# Revit family: Toilet_Seat_Tissue_Dispenser-Bobrick-ClassicSeries-B-3479
name_source: partatom
category: Specialty Equipment
revit_build: Autodesk Revit 2014 (Build: 20130308_1515(x64)
units: mm (PartAtom-declared; Revit-internal decimal feet)

## types (1)
- B-3479
    ADA Compliant = Yes
    Assembly Code = E1010900
    Default Elevation = 60"
    Description = Bobrick ClassicSeries® Surface-Mounted Seat-Cover and Toilet Tissue Dispenser
    Height = 30 7/8"
    Installation Type = Wall Mounted
    Length = 4 3/16"
    Manufacturer = Bobrick Washroom Equipment, Inc.
    Material = Stainless Steel-Bobrick-Type 304-Satin
    Model = B-3479
    Price = Prices may vary. Please consult Manufacturer Representative for most up-to-date price list.
    Product Documentation Link = http://www.bobrick.com
    Product Page URL = http://www.bobrick.com
    Specification = Surface-mounted toilet-seat-cover and toilet tissue dispenser shall be type-304 stainless steel; exposed surfaces shall have satin finish. Toilet tissue dispenser shall be ABS plastic. Flange shall be drawn and beveled, one-piece, seamless construction. Unit shall be mounted on side wall of single toilet compartment. Doors shall be one-piece, seamless construction; secured to unit with a full-length stainless steel piano-hinge; and equipped with tumbler locks keyed like other Bobrick washroom accessories. Toilet-seat-cover dispenser shall hold 500 paper covers. Unit shall be equipped with two theft-resistant, heavy-duty ABS toilet tissue spindles that hold standard-core rolls up to 5-1/4'' (135mm) diameter (1800 sheets). Spindles shall be removable from unit only when door is open. Surface-Mounted Seat-Cover And Toilet Tissue Dispenser shall be Model B-3479 of Bobrick Washroom Equipment, Inc., Clifton Park, New York; Jackson, Tennessee; Los Angeles, California; Bobrick Washroom Equipment Company, Scarborough, Ontario; Bobrick Washroom Equipment Pty. Ltd., Australia; and Bobrick Washroom Equipment Limited, United Kingdom.
    URL = http://www.bobrick.com
    Warranty Information = 1 Year Limited Warranty
    Width = 17 3/16"

## geometry (parser evidence)
native form markers: Sweep x1
no freeform markers — native parametric forms only
